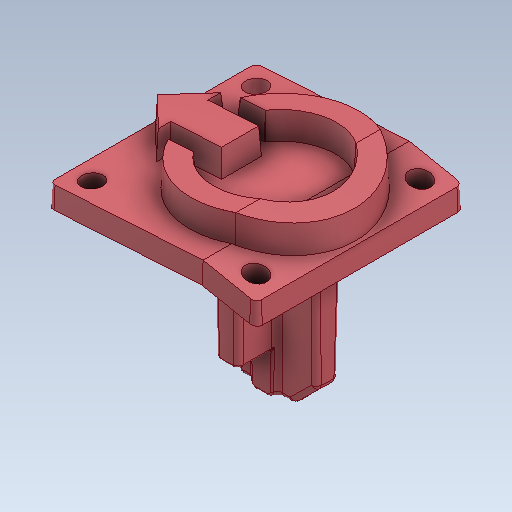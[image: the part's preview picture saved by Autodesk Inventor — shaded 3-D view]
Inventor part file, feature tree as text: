
AUTODESK INVENTOR PART (.ipt)
format: ipt  version: 2020 (Build 240168000, 168)  size: 621,056 bytes
history: native  units: in
note: dims shown in document units (in); Inventor stores cm internally (conversion verified against a paired STEP export)
features: fillet x1
ambient origin geometry x8: Origin, YZ Plane, XZ Plane, XY Plane, X Axis, Y Axis, Z Axis, Center Point
bodies: Solid1 (feature_tree)
feature tree (1):
  fillet  "Fillet4"  [1 undecoded]
note: 1 required parameter value undecoded (feature->parameter linkage not recoverable at this tier; creation-order binding heuristic only, values carry confidence <= 0.55)
